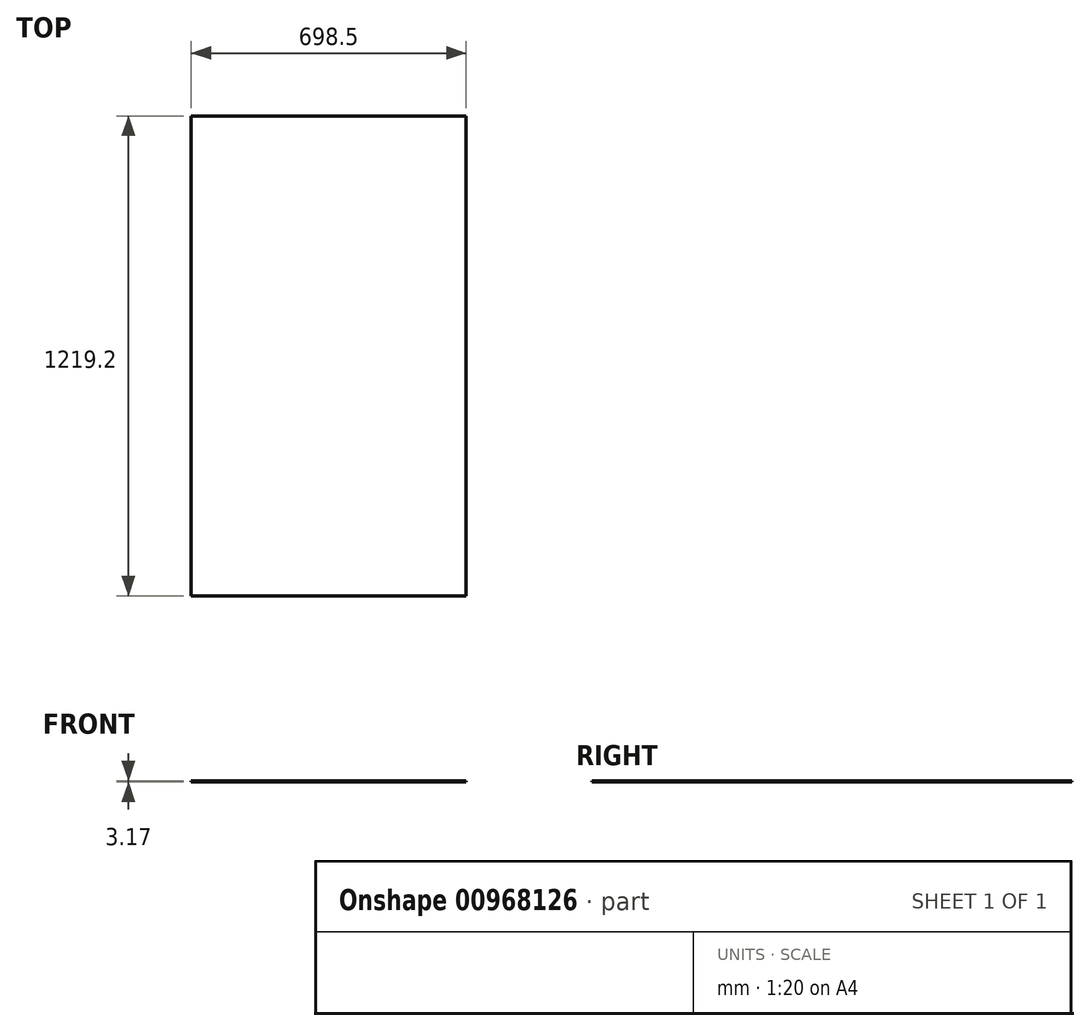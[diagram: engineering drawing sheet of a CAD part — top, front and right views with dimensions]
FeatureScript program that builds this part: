
annotation { "Feature Type Name" : "Feature", "Feature Type Description" : "" }
export const myFeature = defineFeature(function(context is Context, id is Id, definition is map)
    precondition{}
    {
        {
            var Q0;
            Q0=qCreatedBy(makeId("Top.planeOp"),FACE);
            var sketch = newSketch(context, id + "F0", { "sketchPlane" : qUnion([Q0])});
            skLineSegment(sketch, "E0.bottom", {"start": v(349.25, -609.6) * mm, "end": v(-349.25, -609.6) * mm});
            skLineSegment(sketch, "E0.top", {"start": v(349.25, 609.6) * mm, "end": v(-349.25, 609.6) * mm});
            skLineSegment(sketch, "E0.left", {"start": v(349.25, -609.6) * mm, "end": v(349.25, 609.6) * mm});
            skLineSegment(sketch, "E0.right", {"start": v(-349.25, -609.6) * mm, "end": v(-349.25, 609.6) * mm});
            skPoint(sketch, "E0.middle", {"position": v(0, 0) * mm});
            skSolve(sketch);
        }
        {
            var Q0;
            Q0=makeQuery(id+"F0.imprint","IMPRINT",FACE,{"disambiguationData":[TD([[makeQuery(id+"F0.imprint","IMPRINT",EDGE,{"derivedFrom":sQuery(id+"F0.wireOp",EDGE,"E0.bottom")}),-1.0]])]});
            extrude(context, id + "F1", {"entities" : qUnion([Q0]), "depth" : 3.17 * mm, "offsetDistance" : 25.4 * mm});
        }
    });
